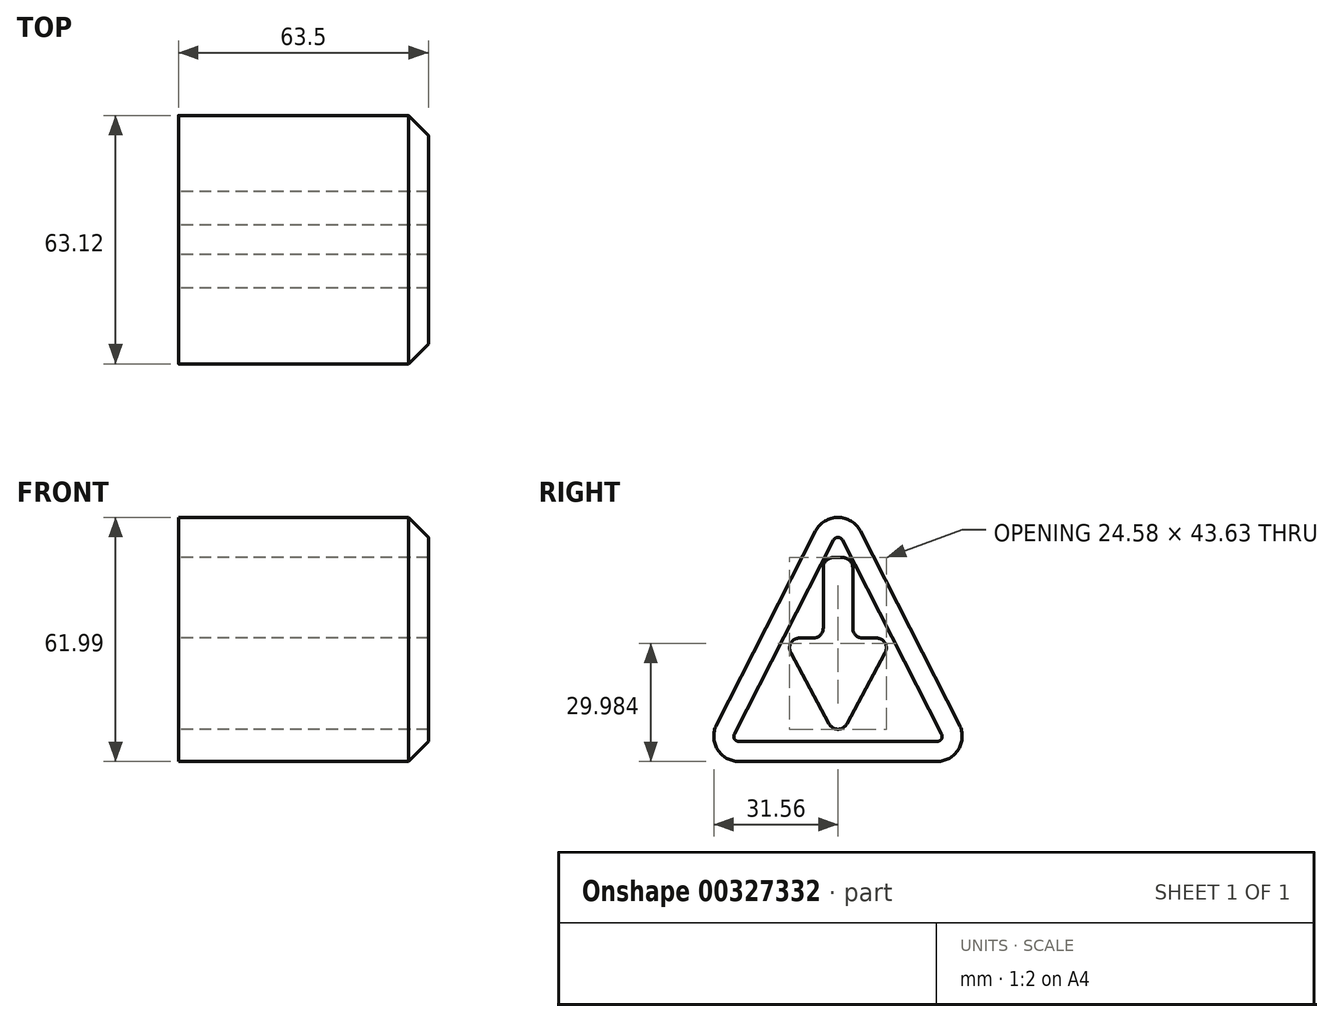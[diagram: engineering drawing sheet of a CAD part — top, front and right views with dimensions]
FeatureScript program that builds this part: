
annotation { "Feature Type Name" : "Feature", "Feature Type Description" : "" }
export const myFeature = defineFeature(function(context is Context, id is Id, definition is map)
    precondition{}
    {
        {
            var Q0;
            Q0=qCreatedBy(makeId("Right.planeOp"),FACE);
            var sketch = newSketch(context, id + "F0", { "sketchPlane" : qUnion([Q0])});
            skLineSegment(sketch, "E0", {"start": v(-25.2, 0) * mm, "end": v(25.2, 0) * mm});
            skLineSegment(sketch, "E1", {"start": v(30.86, 9.24) * mm, "end": v(5.65, 58.54) * mm});
            skLineSegment(sketch, "E2", {"start": v(-5.65, 58.54) * mm, "end": v(-30.86, 9.24) * mm});
            skPoint(sketch, "E3.visualSharp", {"position": v(-35.59, 0) * mm});
            skArc(sketch, "E3.filletArc", {"start": v(-30.86, 9.24) * mm, "mid": v(-30.63, 3.04) * mm, "end": v(-25.2, 0) * mm});
            skPoint(sketch, "E4.visualSharp", {"position": v(0, 69.6) * mm});
            skArc(sketch, "E4.filletArc", {"start": v(5.65, 58.54) * mm, "mid": v(0, 62) * mm, "end": v(-5.65, 58.54) * mm});
            skPoint(sketch, "E5.visualSharp", {"position": v(35.59, 0) * mm});
            skArc(sketch, "E5.filletArc", {"start": v(25.2, 0) * mm, "mid": v(30.63, 3.04) * mm, "end": v(30.86, 9.24) * mm});
            skLineSegment(sketch, "E6", {"start": v(-18.26, 33.89) * mm, "end": v(18.26, 33.89) * mm, "construction": true});
            skLineSegment(sketch, "E7", {"start": v(18.26, 33.89) * mm, "end": v(0, 0) * mm, "construction": true});
            skLineSegment(sketch, "E8", {"start": v(0, 0) * mm, "end": v(-18.26, 33.89) * mm, "construction": true});
            skLineSegment(sketch, "E9.0", {"start": v(-2.24, 9.5) * mm, "end": v(-11.99, 27.6) * mm});
            skLineSegment(sketch, "E9.1", {"start": v(11.99, 27.6) * mm, "end": v(2.24, 9.5) * mm});
            skLineSegment(sketch, "E9.2", {"start": v(-9.75, 31.35) * mm, "end": v(-6.29, 31.35) * mm});
            skPoint(sketch, "E10.visualSharp", {"position": v(-14, 31.35) * mm});
            skArc(sketch, "E10.filletArc", {"start": v(-9.75, 31.35) * mm, "mid": v(-11.93, 30.11) * mm, "end": v(-11.99, 27.6) * mm});
            skPoint(sketch, "E11.visualSharp", {"position": v(0, 5.36) * mm});
            skArc(sketch, "E11.filletArc", {"start": v(-2.24, 9.5) * mm, "mid": v(0, 8.17) * mm, "end": v(2.24, 9.5) * mm});
            skPoint(sketch, "E12.visualSharp", {"position": v(14, 31.35) * mm});
            skArc(sketch, "E12.filletArc", {"start": v(11.99, 27.6) * mm, "mid": v(11.93, 30.11) * mm, "end": v(9.75, 31.35) * mm});
            skLineSegment(sketch, "E13.top", {"start": v(-1.2, 51.8) * mm, "end": v(1.2, 51.8) * mm});
            skLineSegment(sketch, "E13.left", {"start": v(-3.75, 33.89) * mm, "end": v(-3.75, 49.26) * mm});
            skLineSegment(sketch, "E13.right", {"start": v(3.75, 33.89) * mm, "end": v(3.75, 49.26) * mm});
            skLineSegment(sketch, "E14", {"start": v(0, 69.6) * mm, "end": v(0, 0) * mm, "construction": true});
            skLineSegment(sketch, "E15.trimOffspring", {"start": v(6.29, 31.35) * mm, "end": v(9.75, 31.35) * mm});
            skPoint(sketch, "E16.visualSharp", {"position": v(-3.75, 31.35) * mm});
            skArc(sketch, "E16.filletArc", {"start": v(-6.29, 31.35) * mm, "mid": v(-4.5, 32.1) * mm, "end": v(-3.75, 33.89) * mm});
            skPoint(sketch, "E17.visualSharp", {"position": v(3.75, 31.35) * mm});
            skArc(sketch, "E17.filletArc", {"start": v(3.75, 33.89) * mm, "mid": v(4.5, 32.1) * mm, "end": v(6.29, 31.35) * mm});
            skPoint(sketch, "E18.visualSharp", {"position": v(-3.75, 51.8) * mm});
            skArc(sketch, "E18.filletArc", {"start": v(-1.2, 51.8) * mm, "mid": v(-3, 51.05) * mm, "end": v(-3.75, 49.26) * mm});
            skPoint(sketch, "E19.visualSharp", {"position": v(3.75, 51.8) * mm});
            skArc(sketch, "E19.filletArc", {"start": v(3.75, 49.26) * mm, "mid": v(3, 51.05) * mm, "end": v(1.2, 51.8) * mm});
            skSolve(sketch);
        }
        {
            var Q0;
            Q0 = qSketchRegion(id + "F0", true);
            extrude(context, id + "F1", {"entities" : qUnion([Q0]), "depth" : 63.5 * mm});
        }
        {
            var Q0;
            Q0=makeQuery(id+"F1.opExtrude","CAP_EDGE",EDGE,{"disambiguationData":[OSD([sQuery(id+"F0.wireOp",EDGE,"E0")])],"isStart":false});
            chamfer(context, id + "F2", {"entities" : qUnion([Q0]), "width" : 5.08 * mm, "tangentPropagation" : true});
        }
    });
